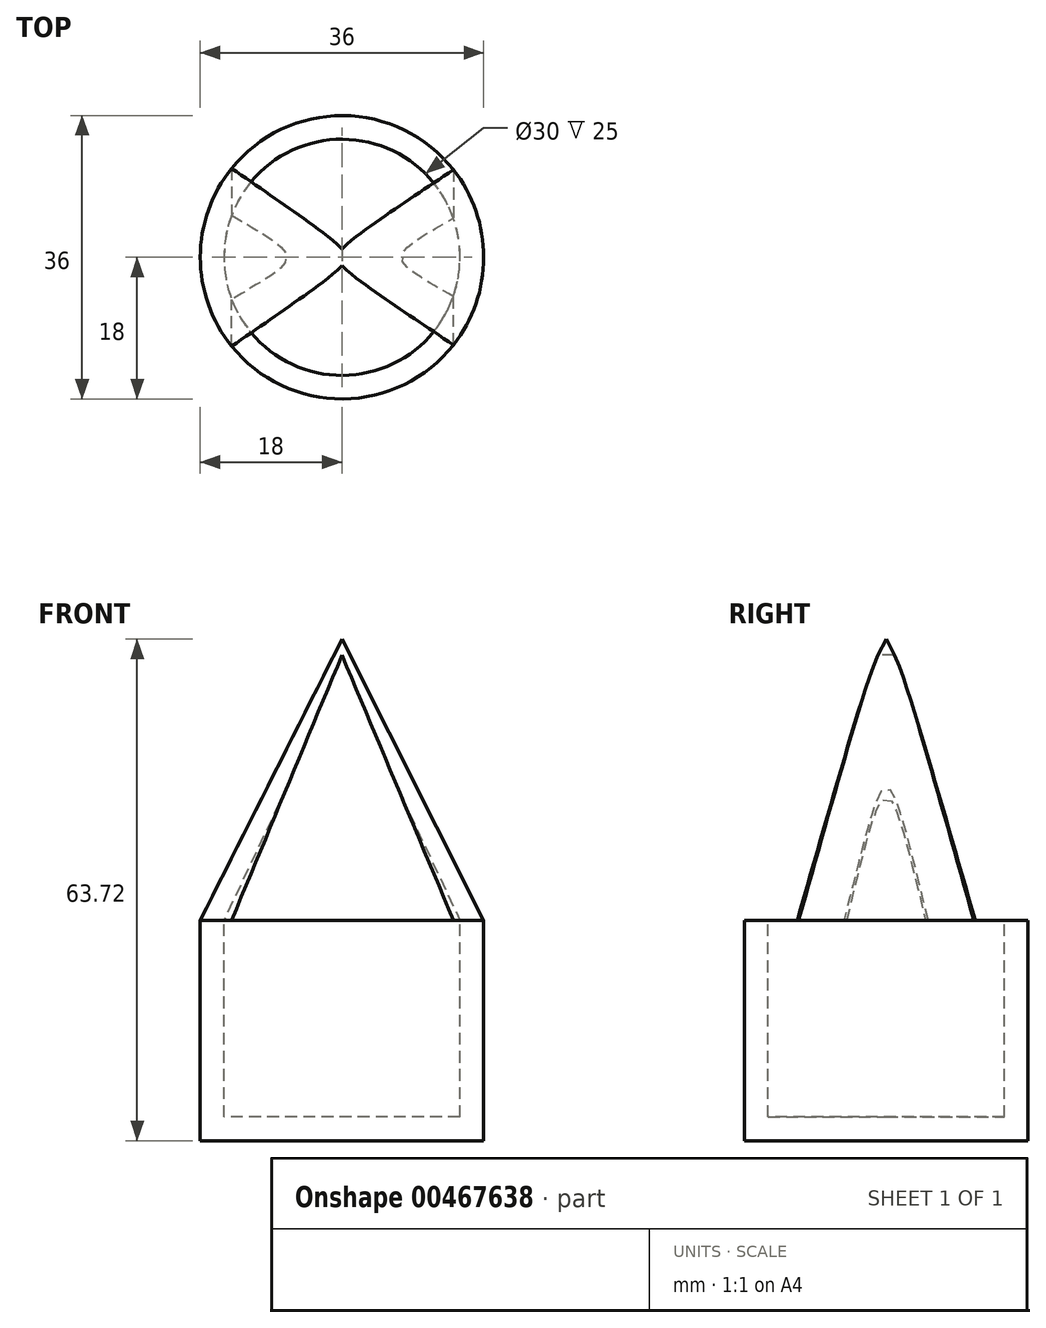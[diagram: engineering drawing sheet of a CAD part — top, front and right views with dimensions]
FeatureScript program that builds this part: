
annotation { "Feature Type Name" : "Feature", "Feature Type Description" : "" }
export const myFeature = defineFeature(function(context is Context, id is Id, definition is map)
    precondition{}
    {
        {
            var Q0;
            Q0=qCreatedBy(makeId("Front.planeOp"),FACE);
            var sketch = newSketch(context, id + "F0", { "sketchPlane" : qUnion([Q0])});
            skLineSegment(sketch, "E0", {"start": v(0, 35.72) * mm, "end": v(-18, 0) * mm});
            skLineSegment(sketch, "E1", {"start": v(-18, 0) * mm, "end": v(-18, -28) * mm});
            skLineSegment(sketch, "E2", {"start": v(-18, -28) * mm, "end": v(0, -28) * mm});
            skLineSegment(sketch, "E3", {"start": v(0, -28) * mm, "end": v(0, -25) * mm});
            skLineSegment(sketch, "E4", {"start": v(0, -25) * mm, "end": v(-15, -25) * mm});
            skLineSegment(sketch, "E5", {"start": v(-15, -25) * mm, "end": v(-15, 0) * mm});
            skLineSegment(sketch, "E6", {"start": v(-15, 0) * mm, "end": v(0, 31.62) * mm});
            skLineSegment(sketch, "E7", {"start": v(0, 31.62) * mm, "end": v(0, 35.72) * mm});
            skLineSegment(sketch, "E8", {"start": v(0, 31.62) * mm, "end": v(0, -25) * mm});
            skSolve(sketch);
        }
        {
            var Q0;
            Q0=makeQuery(id+"F0.imprint","IMPRINT",FACE,{"disambiguationData":[TD([[makeQuery(id+"F0.imprint","IMPRINT",EDGE,{"derivedFrom":sQuery(id+"F0.wireOp",EDGE,"E0")}),1.0]])]});
            var Q1;
            Q1=sQuery(id+"F0.wireOp",EDGE,"E8");
            revolve(context, id + "F1", {"entities" : qUnion([Q0]), "axis" : qUnion([Q1]), "revolveType" : RevolveType.FULL});
        }
        {
            var Q0;
            Q0=qCreatedBy(makeId("Front.planeOp"),FACE);
            var sketch = newSketch(context, id + "F2", { "sketchPlane" : qUnion([Q0])});
            skLineSegment(sketch, "E9", {"start": v(-14.02, 0) * mm, "end": v(14.15, 0) * mm});
            skLineSegment(sketch, "E10", {"start": v(-14.02, 0) * mm, "end": v(0, 33.68) * mm});
            skLineSegment(sketch, "E11", {"start": v(0, 33.68) * mm, "end": v(14.15, 0) * mm});
            skSolve(sketch);
        }
        {
            var Q0;
            Q0 = qSketchRegion(id + "F2", true);
            extrude(context, id + "F3", {"entities" : qUnion([Q0]), "operationType" : NewBodyOperationType.REMOVE, "oppositeDirection" : true, "depth" : 25 * mm});
        }
        {
            var Q0;
            Q0 = qSketchRegion(id + "F2", true);
            extrude(context, id + "F4", {"entities" : qUnion([Q0]), "operationType" : NewBodyOperationType.REMOVE, "depth" : 25 * mm});
        }
    });
